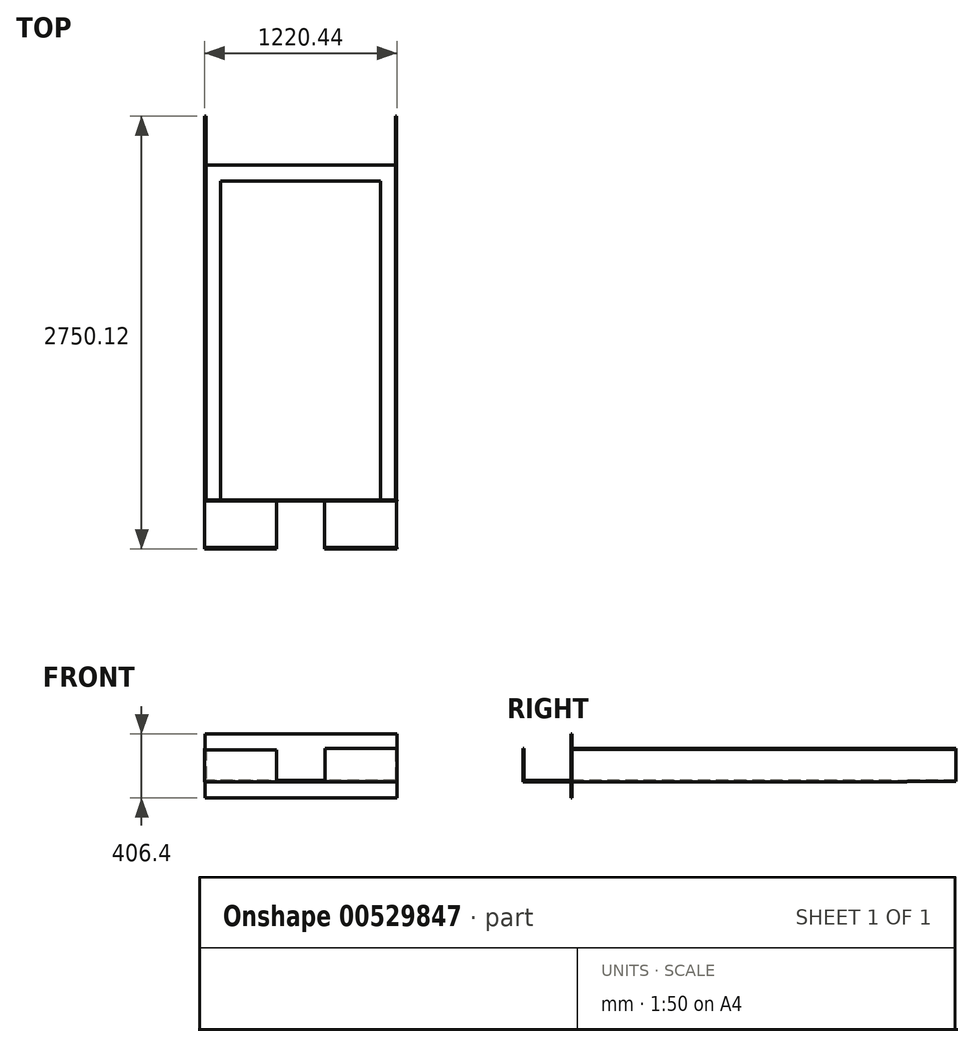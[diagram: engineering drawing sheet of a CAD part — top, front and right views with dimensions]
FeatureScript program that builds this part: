
annotation { "Feature Type Name" : "Feature", "Feature Type Description" : "" }
export const myFeature = defineFeature(function(context is Context, id is Id, definition is map)
    precondition{}
    {
        {
            var Q0;
            Q0=qCreatedBy(makeId("Top.planeOp"),FACE);
            var sketch = newSketch(context, id + "F0", { "sketchPlane" : qUnion([Q0])});
            skLineSegment(sketch, "E0.bottom", {"start": v(609.6, -1219.2) * mm, "end": v(-609.6, -1219.2) * mm});
            skLineSegment(sketch, "E0.top", {"start": v(609.6, 1219.2) * mm, "end": v(-609.6, 1219.2) * mm});
            skLineSegment(sketch, "E0.left", {"start": v(609.6, -1219.2) * mm, "end": v(609.6, 1219.2) * mm});
            skLineSegment(sketch, "E0.right", {"start": v(-609.6, -1219.2) * mm, "end": v(-609.6, 1219.2) * mm});
            skPoint(sketch, "E0.middle", {"position": v(0, 0) * mm});
            skLineSegment(sketch, "E1.bottom", {"start": v(-508, 1117.6) * mm, "end": v(508, 1117.6) * mm});
            skLineSegment(sketch, "E1.top", {"start": v(-508, -914.4) * mm, "end": v(508, -914.4) * mm});
            skLineSegment(sketch, "E1.left", {"start": v(-508, 1117.6) * mm, "end": v(-508, -914.4) * mm});
            skLineSegment(sketch, "E1.right", {"start": v(508, 1117.6) * mm, "end": v(508, -914.4) * mm});
            skSolve(sketch);
        }
        {
            var Q0;
            Q0 = qSketchRegion(id + "F0", true);
            extrude(context, id + "F1", {"entities" : qUnion([Q0]), "depth" : 9.52 * mm, "offsetDistance" : 25.4 * mm});
        }
        {
            var Q0;
            Q0 = qSketchRegion(id + "F0", true);
            var Q1;
            Q1 = qSketchRegion(id + "FhVFl5MjGz4tcW9_1", true);
            extrude(context, id + "F2", {"entities" : qUnion([Q0, Q1]), "operationType" : NewBodyOperationType.REMOVE, "oppositeDirection" : true, "depth" : 9.52 * mm, "offsetDistance" : 25.4 * mm});
        }
        {
            var Q0;
            Q0=qCreatedBy(makeId("Front.planeOp"),FACE);
            var sketch = newSketch(context, id + "F3", { "sketchPlane" : qUnion([Q0])});
            skLineSegment(sketch, "E2.bottom", {"start": v(-608.37, 304.8) * mm, "end": v(610.83, 304.8) * mm});
            skLineSegment(sketch, "E2.top", {"start": v(-608.37, -101.6) * mm, "end": v(610.83, -101.6) * mm});
            skLineSegment(sketch, "E2.left", {"start": v(-608.37, 304.8) * mm, "end": v(-608.37, -101.6) * mm});
            skLineSegment(sketch, "E2.right", {"start": v(610.83, 304.8) * mm, "end": v(610.83, -101.6) * mm});
            skSolve(sketch);
        }
        {
            var Q0;
            Q0=makeQuery(id+"F3.imprint","IMPRINT",FACE,{"disambiguationData":[TD([[makeQuery(id+"F3.imprint","IMPRINT",EDGE,{"derivedFrom":sQuery(id+"F3.wireOp",EDGE,"E2.bottom")}),-1.0]])]});
            extrude(context, id + "F4", {"entities" : qUnion([Q0]), "operationType" : NewBodyOperationType.ADD, "depth" : 914.4 * mm, "offsetDistance" : 25.4 * mm, "hasSecondDirection" : true, "secondDirectionOppositeDirection" : false, "secondDirectionDepth" : 908.05 * mm});
        }
        {
            var Q0;
            Q0=qCreatedBy(makeId("Right.planeOp"),FACE);
            var sketch = newSketch(context, id + "F5", { "sketchPlane" : qUnion([Q0])});
            skLineSegment(sketch, "E3.bottom", {"start": v(1530.7, 206.8) * mm, "end": v(-907.7, 206.8) * mm});
            skLineSegment(sketch, "E3.top", {"start": v(1530.7, 3.6) * mm, "end": v(-907.7, 3.6) * mm});
            skLineSegment(sketch, "E3.left", {"start": v(1530.7, 206.8) * mm, "end": v(1530.7, 3.6) * mm});
            skLineSegment(sketch, "E3.right", {"start": v(-907.7, 206.8) * mm, "end": v(-907.7, 3.6) * mm});
            skSolve(sketch);
        }
        {
            var Q0;
            Q0=makeQuery(id+"F5.imprint","IMPRINT",FACE,{"disambiguationData":[TD([[makeQuery(id+"F5.imprint","IMPRINT",EDGE,{"derivedFrom":sQuery(id+"F5.wireOp",EDGE,"E3.bottom")}),1.0]])]});
            extrude(context, id + "F6", {"entities" : qUnion([Q0]), "operationType" : NewBodyOperationType.ADD, "depth" : 609.6 * mm, "offsetDistance" : 25.4 * mm, "hasSecondDirection" : true, "secondDirectionOppositeDirection" : false, "secondDirectionDepth" : 601.35 * mm});
        }
        {
            var Q0;
            Q0=qCreatedBy(makeId("Right.planeOp"),FACE);
            var sketch = newSketch(context, id + "F7", { "sketchPlane" : qUnion([Q0])});
            skLineSegment(sketch, "E4.bottom", {"start": v(1530.92, 212.06) * mm, "end": v(-907.48, 212.06) * mm});
            skLineSegment(sketch, "E4.top", {"start": v(1530.92, 8.86) * mm, "end": v(-907.48, 8.86) * mm});
            skLineSegment(sketch, "E4.left", {"start": v(1530.92, 212.06) * mm, "end": v(1530.92, 8.86) * mm});
            skLineSegment(sketch, "E4.right", {"start": v(-907.48, 212.06) * mm, "end": v(-907.48, 8.86) * mm});
            skSolve(sketch);
        }
        {
            var Q0;
            Q0 = qSketchRegion(id + "F7", true);
            extrude(context, id + "F8", {"entities" : qUnion([Q0]), "operationType" : NewBodyOperationType.ADD, "oppositeDirection" : true, "depth" : 609.6 * mm, "offsetDistance" : 25.4 * mm, "hasSecondDirection" : true, "secondDirectionOppositeDirection" : true, "secondDirectionDepth" : 601.35 * mm});
        }
        {
            var Q0;
            Q0=qCreatedBy(makeId("Front.planeOp"),FACE);
            var sketch = newSketch(context, id + "F9", { "sketchPlane" : qUnion([Q0])});
            skLineSegment(sketch, "E5.bottom", {"start": v(-609.61, 202.81) * mm, "end": v(-152.41, 202.81) * mm});
            skLineSegment(sketch, "E5.top", {"start": v(-609.61, -0.39) * mm, "end": v(-152.41, -0.39) * mm});
            skLineSegment(sketch, "E5.left", {"start": v(-609.61, 202.81) * mm, "end": v(-609.61, -0.39) * mm});
            skLineSegment(sketch, "E5.right", {"start": v(-152.41, 202.81) * mm, "end": v(-152.41, -0.39) * mm});
            skSolve(sketch);
        }
        {
            var Q0;
            Q0=qCreatedBy(makeId("Top.planeOp"),FACE);
            var sketch = newSketch(context, id + "F10", { "sketchPlane" : qUnion([Q0])});
            skLineSegment(sketch, "E6.bottom", {"start": v(-152.4, -914.72) * mm, "end": v(152.4, -914.72) * mm});
            skLineSegment(sketch, "E6.top", {"start": v(-152.4, -1219.52) * mm, "end": v(152.4, -1219.52) * mm});
            skLineSegment(sketch, "E6.left", {"start": v(-152.4, -914.72) * mm, "end": v(-152.4, -1219.52) * mm});
            skLineSegment(sketch, "E6.right", {"start": v(152.4, -914.72) * mm, "end": v(152.4, -1219.52) * mm});
            skSolve(sketch);
        }
        {
            var Q0;
            Q0=makeQuery(id+"F10.imprint","IMPRINT",FACE,{"disambiguationData":[TD([[makeQuery(id+"F10.imprint","IMPRINT",EDGE,{"derivedFrom":sQuery(id+"F10.wireOp",EDGE,"E6.bottom")}),-1.0]])]});
            extrude(context, id + "F11", {"entities" : qUnion([Q0]), "operationType" : NewBodyOperationType.REMOVE, "depth" : 43.18 * mm, "offsetDistance" : 25.4 * mm});
        }
        {
            var Q0;
            Q0 = qSketchRegion(id + "F9", true);
            extrude(context, id + "F12", {"entities" : qUnion([Q0]), "operationType" : NewBodyOperationType.ADD, "depth" : 1219.2 * mm, "offsetDistance" : 25.4 * mm, "hasSecondDirection" : true, "secondDirectionOppositeDirection" : false, "secondDirectionDepth" : 1210.94 * mm});
        }
        {
            var Q0;
            Q0=qCreatedBy(makeId("Front.planeOp"),FACE);
            var sketch = newSketch(context, id + "F13", { "sketchPlane" : qUnion([Q0])});
            skLineSegment(sketch, "E7.bottom", {"start": v(153.58, 211.89) * mm, "end": v(610.78, 211.89) * mm});
            skLineSegment(sketch, "E7.top", {"start": v(153.58, 8.69) * mm, "end": v(610.78, 8.69) * mm});
            skLineSegment(sketch, "E7.left", {"start": v(153.58, 211.89) * mm, "end": v(153.58, 8.69) * mm});
            skLineSegment(sketch, "E7.right", {"start": v(610.78, 211.89) * mm, "end": v(610.78, 8.69) * mm});
            skSolve(sketch);
        }
        {
            var Q0;
            Q0 = qSketchRegion(id + "F13", true);
            extrude(context, id + "F14", {"entities" : qUnion([Q0]), "operationType" : NewBodyOperationType.ADD, "depth" : 1219.2 * mm, "offsetDistance" : 25.4 * mm, "hasSecondDirection" : true, "secondDirectionOppositeDirection" : false, "secondDirectionDepth" : 1210.94 * mm});
        }
    });
